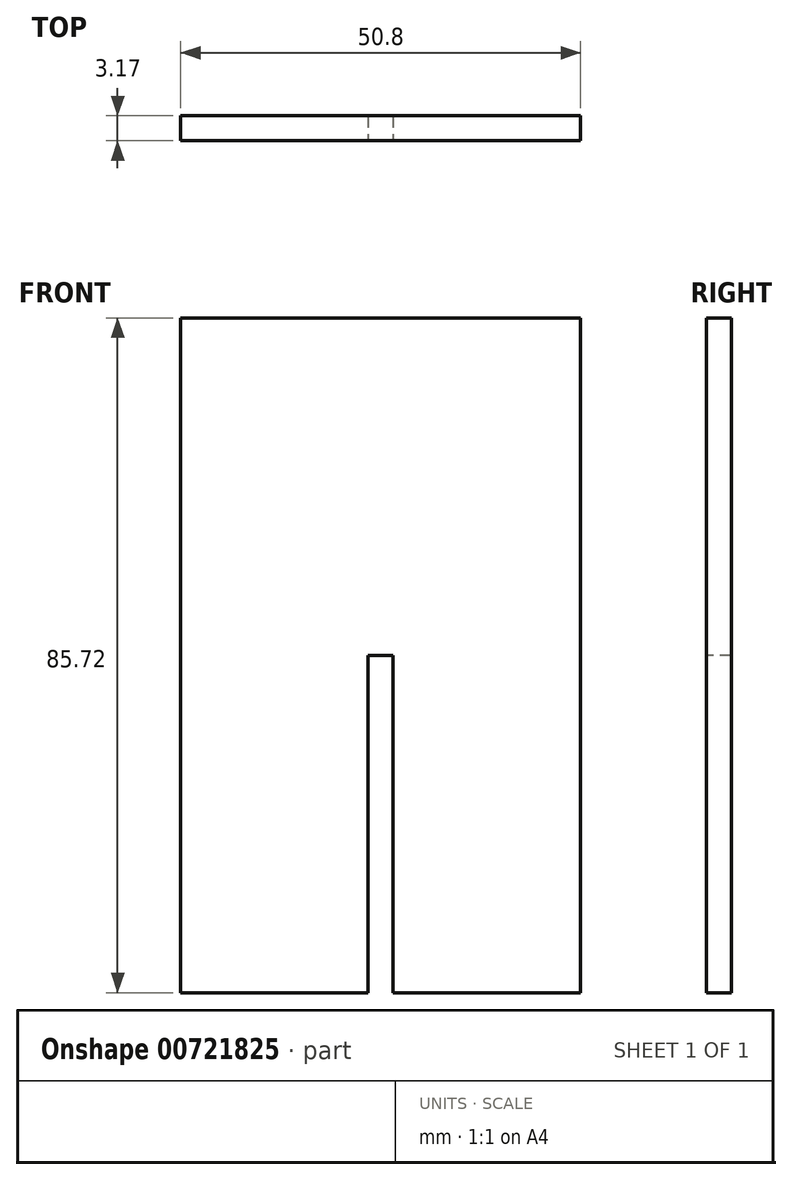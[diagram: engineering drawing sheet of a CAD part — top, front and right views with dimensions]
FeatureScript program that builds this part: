
annotation { "Feature Type Name" : "Feature", "Feature Type Description" : "" }
export const myFeature = defineFeature(function(context is Context, id is Id, definition is map)
    precondition{}
    {
        {
            var Q0;
            Q0=qCreatedBy(makeId("Front.planeOp"),FACE);
            var sketch = newSketch(context, id + "F0", { "sketchPlane" : qUnion([Q0])});
            skLineSegment(sketch, "E0.bottom", {"start": v(32.34, 42.86) * mm, "end": v(-18.46, 42.86) * mm});
            skLineSegment(sketch, "E0.top", {"start": v(32.34, -42.86) * mm, "end": v(-18.46, -42.86) * mm});
            skLineSegment(sketch, "E0.left", {"start": v(32.34, 42.86) * mm, "end": v(32.34, -42.86) * mm});
            skLineSegment(sketch, "E0.right", {"start": v(-18.46, 42.86) * mm, "end": v(-18.46, -42.86) * mm});
            skPoint(sketch, "E0.middle", {"position": v(6.94, 0) * mm});
            skSolve(sketch);
        }
        {
            var Q0;
            Q0=qSketchRegion(id+"F0",true);
            extrude(context, id + "F1", {"entities" : qUnion([Q0]), "depth" : 3.17 * mm, "offsetDistance" : 25.4 * mm});
        }
        {
            var Q0;
            Q0=makeQuery(id+"F1.opExtrude","CAP_FACE",FACE,{"disambiguationData":[OSD([sQuery(id+"F0.wireOp",EDGE,"E0.bottom"),sQuery(id+"F0.wireOp",EDGE,"E0.top"),sQuery(id+"F0.wireOp",EDGE,"E0.left"),sQuery(id+"F0.wireOp",EDGE,"E0.right")])],"isStart":false});
            var sketch = newSketch(context, id + "F2", { "sketchPlane" : qUnion([Q0])});
            skLineSegment(sketch, "E1.bottom", {"start": v(5.35, -42.86) * mm, "end": v(8.53, -42.86) * mm});
            skLineSegment(sketch, "E1.top", {"start": v(5.35, 0) * mm, "end": v(8.53, 0) * mm});
            skLineSegment(sketch, "E1.left", {"start": v(5.35, -42.86) * mm, "end": v(5.35, 0) * mm});
            skLineSegment(sketch, "E1.right", {"start": v(8.53, -42.86) * mm, "end": v(8.53, 0) * mm});
            skSolve(sketch);
        }
        {
            var Q0;
            Q0=qSketchRegion(id+"F2",true);
            extrude(context, id + "F3", {"entities" : qUnion([Q0]), "operationType" : NewBodyOperationType.REMOVE, "endBound" : BoundingType.THROUGH_ALL, "oppositeDirection" : true, "depth" : 25.4 * mm, "offsetDistance" : 25.4 * mm});
        }
    });
